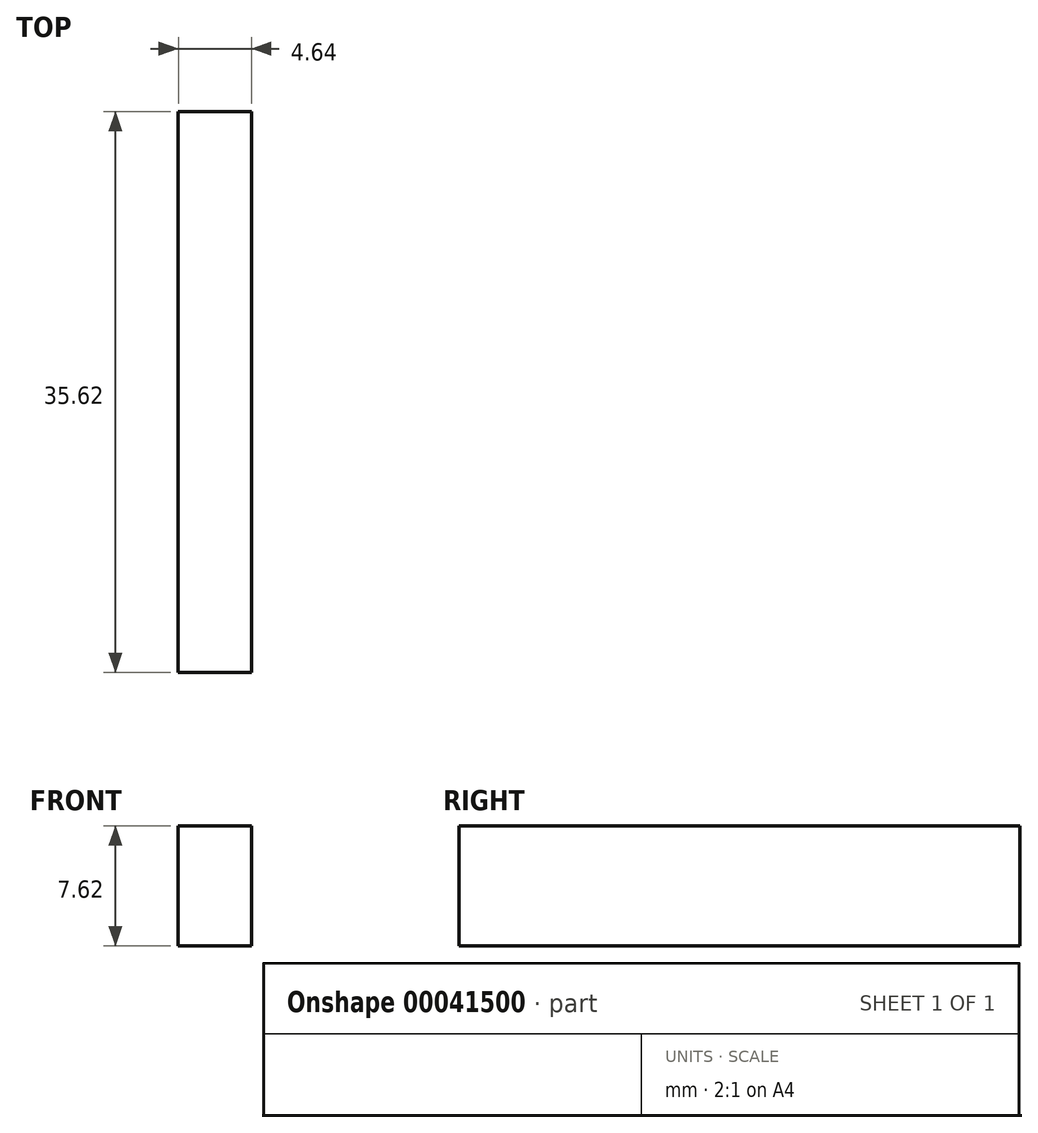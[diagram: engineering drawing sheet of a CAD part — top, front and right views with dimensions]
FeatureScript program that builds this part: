
annotation { "Feature Type Name" : "Feature", "Feature Type Description" : "" }
export const myFeature = defineFeature(function(context is Context, id is Id, definition is map)
    precondition{}
    {
        {
            var Q0;
            Q0=qCreatedBy(makeId("Top.planeOp"),FACE);
            var sketch = newSketch(context, id + "F0", { "sketchPlane" : qUnion([Q0])});
            skLineSegment(sketch, "E0", {"start": v(0, 35.62) * mm, "end": v(-4.64, 35.62) * mm});
            skLineSegment(sketch, "E1", {"start": v(-4.64, 35.62) * mm, "end": v(-4.64, 0) * mm});
            skLineSegment(sketch, "E2", {"start": v(-4.64, 0) * mm, "end": v(0, 0) * mm});
            skLineSegment(sketch, "E3", {"start": v(0, 0) * mm, "end": v(0, 35.62) * mm});
            skSolve(sketch);
        }
        {
            var Q0;
            Q0=makeQuery(id+"F0.imprint","IMPRINT",FACE,{"disambiguationData":[TD([[makeQuery(id+"F0.imprint","IMPRINT",EDGE,{"derivedFrom":sQuery(id+"F0.wireOp",EDGE,"E0")}),1.0]])]});
            extrude(context, id + "F1", {"entities" : qUnion([Q0]), "endBound" : BoundingType.SYMMETRIC, "depth" : 7.62 * mm});
        }
    });
